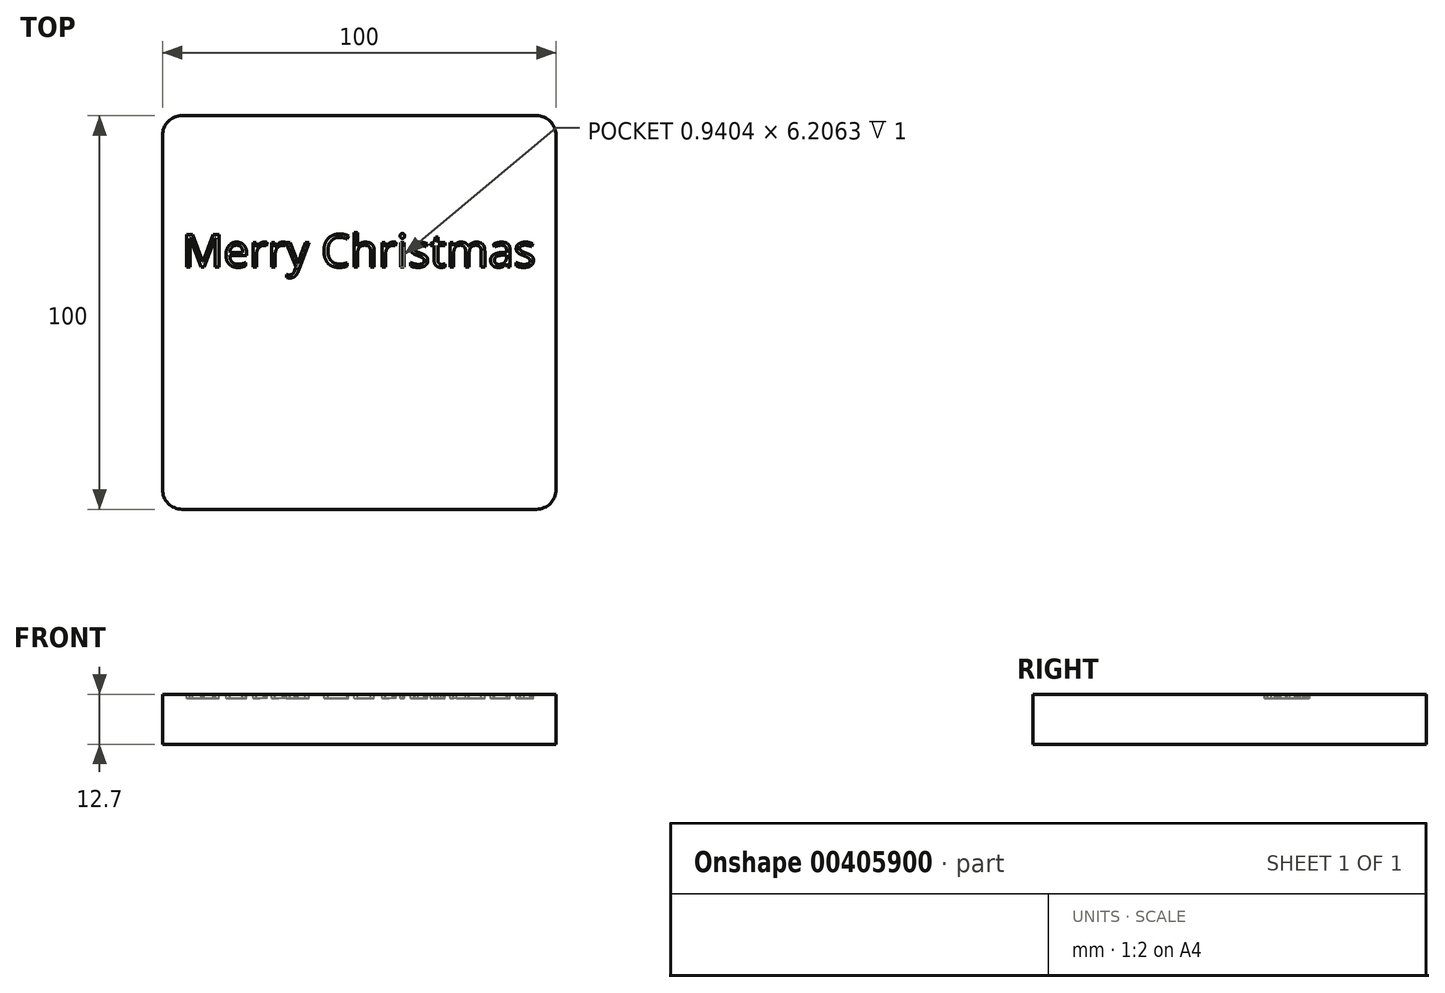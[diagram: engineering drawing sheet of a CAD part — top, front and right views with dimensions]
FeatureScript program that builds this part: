
annotation { "Feature Type Name" : "Feature", "Feature Type Description" : "" }
export const myFeature = defineFeature(function(context is Context, id is Id, definition is map)
    precondition{}
    {
        {
            var Q0;
            Q0=qCreatedBy(makeId("Top.planeOp"),FACE);
            var sketch = newSketch(context, id + "F0", { "sketchPlane" : qUnion([Q0])});
            skLineSegment(sketch, "E0.bottom", {"start": v(50, 50) * mm, "end": v(-50, 50) * mm});
            skLineSegment(sketch, "E0.top", {"start": v(50, -50) * mm, "end": v(-50, -50) * mm});
            skLineSegment(sketch, "E0.left", {"start": v(50, 50) * mm, "end": v(50, -50) * mm});
            skLineSegment(sketch, "E0.right", {"start": v(-50, 50) * mm, "end": v(-50, -50) * mm});
            skPoint(sketch, "E0.middle", {"position": v(0, 0) * mm});
            skSolve(sketch);
        }
        {
            var Q0;
            Q0 = qSketchRegion(id + "F0", true);
            extrude(context, id + "F1", {"entities" : qUnion([Q0]), "depth" : 12.7 * mm});
        }
        {
            var Q0;
            Q0=makeQuery(id+"F1.opExtrude","SWEPT_EDGE",EDGE,{"disambiguationData":[OSD([sQuery(id+"F0.wireOp",EDGE,"E0.top"),sQuery(id+"F0.wireOp",EDGE,"E0.left")])]});
            var Q1;
            Q1=makeQuery(id+"F1.opExtrude","SWEPT_EDGE",EDGE,{"disambiguationData":[OSD([sQuery(id+"F0.wireOp",EDGE,"E0.top"),sQuery(id+"F0.wireOp",EDGE,"E0.right")])]});
            var Q2;
            Q2=makeQuery(id+"F1.opExtrude","SWEPT_EDGE",EDGE,{"disambiguationData":[OSD([sQuery(id+"F0.wireOp",EDGE,"E0.bottom"),sQuery(id+"F0.wireOp",EDGE,"E0.right")])]});
            var Q3;
            Q3=makeQuery(id+"F1.opExtrude","SWEPT_EDGE",EDGE,{"disambiguationData":[OSD([sQuery(id+"F0.wireOp",EDGE,"E0.bottom"),sQuery(id+"F0.wireOp",EDGE,"E0.left")])]});
            fillet(context, id + "F2", {"entities" : qUnion([Q0, Q1, Q2, Q3]), "radius" : 5 * mm, "tangentPropagation" : true, "allowEdgeOverflow" : false});
        }
        {
            var Q0;
            Q0=makeQuery(id+"F1.opExtrude","CAP_FACE",FACE,{"disambiguationData":[OSD([sQuery(id+"F0.wireOp",EDGE,"E0.bottom"),sQuery(id+"F0.wireOp",EDGE,"E0.top"),sQuery(id+"F0.wireOp",EDGE,"E0.left"),sQuery(id+"F0.wireOp",EDGE,"E0.right")])],"isStart":false});
            var sketch = newSketch(context, id + "F3", { "sketchPlane" : qUnion([Q0])});
            skText(sketch, "E1", { "text": "Merry Christmas", "fontName": "OpenSans-Regular.ttf"});
            const initialGuessF3  = {"E1": [-0.045, 0.01155, 1, 0, 0.00835]};
            skSetInitialGuess(sketch, initialGuessF3);
            skSolve(sketch);
        }
        {
            var Q0;
            Q0 = qSketchRegion(id + "F3", true);
            extrude(context, id + "F4", {"entities" : qUnion([Q0]), "operationType" : NewBodyOperationType.REMOVE, "oppositeDirection" : true, "depth" : 1 * mm});
        }
    });
